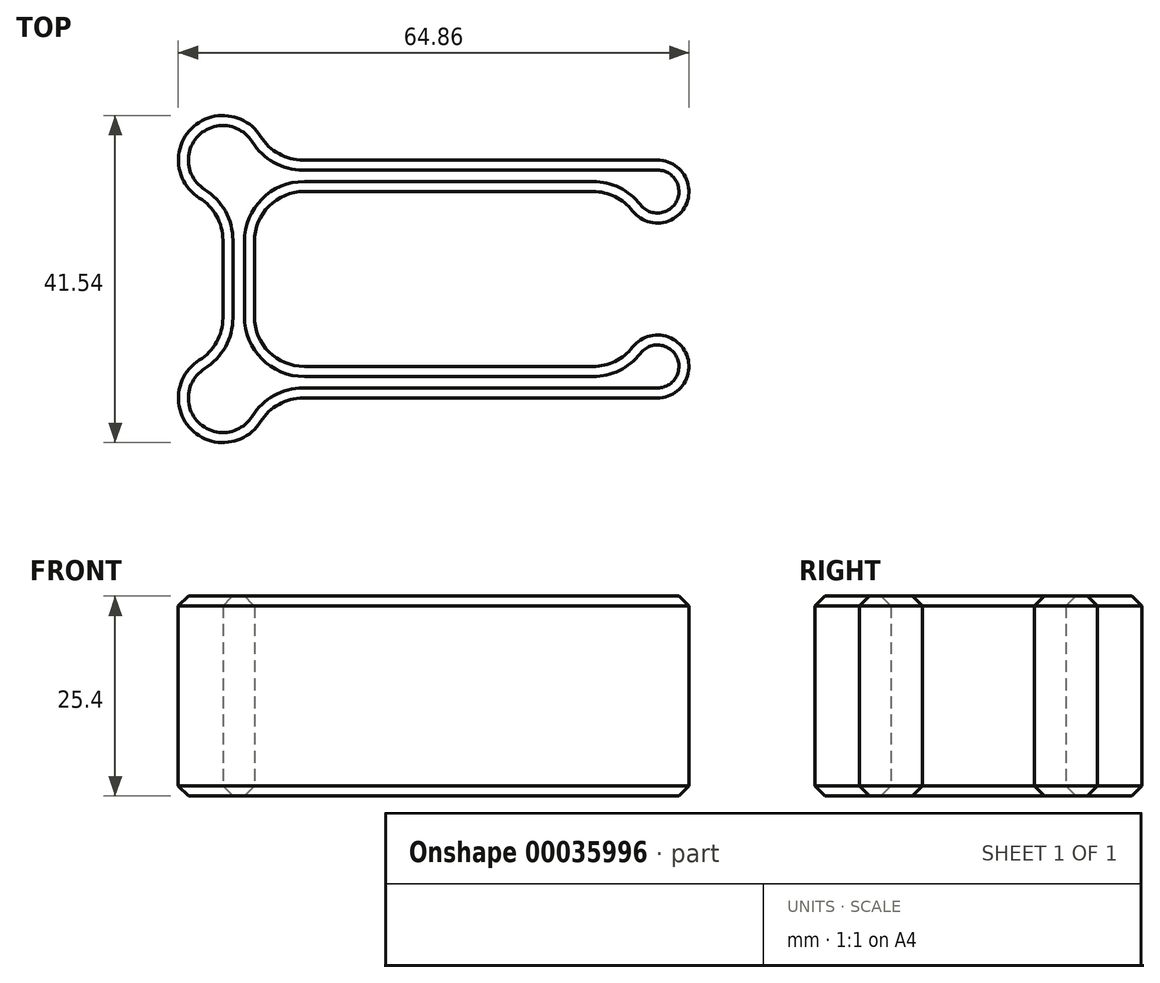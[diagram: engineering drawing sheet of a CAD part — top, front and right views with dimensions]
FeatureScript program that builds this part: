
annotation { "Feature Type Name" : "Feature", "Feature Type Description" : "" }
export const myFeature = defineFeature(function(context is Context, id is Id, definition is map)
    precondition{}
    {
        {
            var Q0;
            Q0=qCreatedBy(makeId("Top.planeOp"),FACE);
            var sketch = newSketch(context, id + "F0", { "sketchPlane" : qUnion([Q0])});
            skLineSegment(sketch, "E0.rect.right", {"start": v(-75.55, 24.4) * mm, "end": v(-75.55, 33.92) * mm});
            skPoint(sketch, "E0.rect.middle", {"position": v(-49.95, 29.16) * mm});
            skArc(sketch, "E1", {"start": v(-74.75, 47.26) * mm, "mid": v(-83.55, 48.27) * mm, "end": v(-82.54, 39.47) * mm});
            skLineSegment(sketch, "E2", {"start": v(-24.35, 44.27) * mm, "end": v(-69.36, 44.27) * mm});
            skLineSegment(sketch, "E3", {"start": v(-32.52, 40.27) * mm, "end": v(-69.2, 40.27) * mm});
            skLineSegment(sketch, "E4", {"start": v(-79.55, 24.24) * mm, "end": v(-79.55, 34.08) * mm});
            skArc(sketch, "E5", {"start": v(-82.54, 18.85) * mm, "mid": v(-83.55, 10.05) * mm, "end": v(-74.75, 11.06) * mm});
            skLineSegment(sketch, "E6", {"start": v(-32.52, 18.05) * mm, "end": v(-69.2, 18.05) * mm});
            skLineSegment(sketch, "E7", {"start": v(-24.35, 14.05) * mm, "end": v(-69.36, 14.05) * mm});
            skArc(sketch, "E8", {"start": v(-27.5, 37.82) * mm, "mid": v(-20.76, 38.51) * mm, "end": v(-24.35, 44.27) * mm});
            skArc(sketch, "E9", {"start": v(-24.35, 14.05) * mm, "mid": v(-20.76, 19.8) * mm, "end": v(-27.5, 20.5) * mm});
            skPoint(sketch, "E10.visualSharp", {"position": v(-73.9, 44.27) * mm});
            skArc(sketch, "E10.filletArc", {"start": v(-74.75, 47.26) * mm, "mid": v(-72.44, 45.07) * mm, "end": v(-69.36, 44.27) * mm});
            skPoint(sketch, "E11.visualSharp", {"position": v(-79.55, 38.62) * mm});
            skArc(sketch, "E11.filletArc", {"start": v(-79.55, 34.08) * mm, "mid": v(-80.35, 37.16) * mm, "end": v(-82.54, 39.47) * mm});
            skPoint(sketch, "E12.visualSharp", {"position": v(-79.55, 19.7) * mm});
            skArc(sketch, "E12.filletArc", {"start": v(-82.54, 18.85) * mm, "mid": v(-80.35, 21.16) * mm, "end": v(-79.55, 24.24) * mm});
            skPoint(sketch, "E13.visualSharp", {"position": v(-73.9, 14.05) * mm});
            skArc(sketch, "E13.filletArc", {"start": v(-69.36, 14.05) * mm, "mid": v(-72.44, 13.25) * mm, "end": v(-74.75, 11.06) * mm});
            skPoint(sketch, "E14.visualSharp", {"position": v(-75.55, 18.05) * mm});
            skArc(sketch, "E14.filletArc", {"start": v(-75.55, 24.4) * mm, "mid": v(-73.69, 19.9) * mm, "end": v(-69.2, 18.05) * mm});
            skPoint(sketch, "E15.visualSharp", {"position": v(-75.55, 40.27) * mm});
            skArc(sketch, "E15.filletArc", {"start": v(-69.2, 40.27) * mm, "mid": v(-73.69, 38.41) * mm, "end": v(-75.55, 33.92) * mm});
            skPoint(sketch, "E16.visualSharp", {"position": v(-28.35, 40.27) * mm});
            skArc(sketch, "E16.filletArc", {"start": v(-27.5, 37.82) * mm, "mid": v(-29.73, 39.63) * mm, "end": v(-32.52, 40.27) * mm});
            skPoint(sketch, "E17.visualSharp", {"position": v(-28.35, 18.05) * mm});
            skArc(sketch, "E17.filletArc", {"start": v(-32.52, 18.05) * mm, "mid": v(-29.73, 18.7) * mm, "end": v(-27.5, 20.5) * mm});
            skSolve(sketch);
        }
        {
            var Q0;
            Q0=makeQuery(id+"F0.imprint","IMPRINT",FACE,{"disambiguationData":[TD([[makeQuery(id+"F0.imprint","IMPRINT",EDGE,{"derivedFrom":sQuery(id+"F0.wireOp",EDGE,"E0.rect.right")}),1.0]])]});
            extrude(context, id + "F1", {"entities" : qUnion([Q0]), "depth" : 25.4 * mm});
        }
        {
            var Q0;
            Q0=makeQuery(id+"F1.opExtrude","CAP_EDGE",EDGE,{"disambiguationData":[OSD([sQuery(id+"F0.wireOp",EDGE,"E4")])],"isStart":false});
            var Q1;
            Q1=makeQuery(id+"F1.opExtrude","CAP_EDGE",EDGE,{"disambiguationData":[OSD([sQuery(id+"F0.wireOp",EDGE,"E12.filletArc")])],"isStart":false});
            var Q2;
            Q2=makeQuery(id+"F1.opExtrude","CAP_EDGE",EDGE,{"disambiguationData":[OSD([sQuery(id+"F0.wireOp",EDGE,"E3")])],"isStart":false});
            var Q3;
            Q3=makeQuery(id+"F1.opExtrude","CAP_EDGE",EDGE,{"disambiguationData":[OSD([sQuery(id+"F0.wireOp",EDGE,"E2")])],"isStart":false});
            var Q4;
            Q4=makeQuery(id+"F1.opExtrude","CAP_EDGE",EDGE,{"disambiguationData":[OSD([sQuery(id+"F0.wireOp",EDGE,"E6")])],"isStart":false});
            var Q5;
            Q5=makeQuery(id+"F1.opExtrude","CAP_EDGE",EDGE,{"disambiguationData":[OSD([sQuery(id+"F0.wireOp",EDGE,"E5")])],"isStart":false});
            var Q6;
            Q6=makeQuery(id+"F1.opExtrude","CAP_EDGE",EDGE,{"disambiguationData":[OSD([sQuery(id+"F0.wireOp",EDGE,"E1")])],"isStart":true});
            var Q7;
            Q7=makeQuery(id+"F1.opExtrude","CAP_EDGE",EDGE,{"disambiguationData":[OSD([sQuery(id+"F0.wireOp",EDGE,"E5")])],"isStart":true});
            var Q8;
            Q8=makeQuery(id+"F1.opExtrude","CAP_EDGE",EDGE,{"disambiguationData":[OSD([sQuery(id+"F0.wireOp",EDGE,"E4")])],"isStart":true});
            var Q9;
            Q9=makeQuery(id+"F1.opExtrude","SWEPT_EDGE",EDGE,{"disambiguationData":[OSD([sQuery(id+"F0.wireOp",EDGE,"E1"),sQuery(id+"F0.wireOp",EDGE,"E11.filletArc")])]});
            var Q10;
            Q10=makeQuery(id+"F1.opExtrude","CAP_EDGE",EDGE,{"disambiguationData":[OSD([sQuery(id+"F0.wireOp",EDGE,"E12.filletArc")])],"isStart":true});
            var Q11;
            Q11=makeQuery(id+"F1.opExtrude","SWEPT_EDGE",EDGE,{"disambiguationData":[OSD([sQuery(id+"F0.wireOp",EDGE,"E2"),sQuery(id+"F0.wireOp",EDGE,"E8")])]});
            var Q12;
            Q12=makeQuery(id+"F1.opExtrude","CAP_EDGE",EDGE,{"disambiguationData":[OSD([sQuery(id+"F0.wireOp",EDGE,"E17.filletArc")])],"isStart":false});
            var Q13;
            Q13=makeQuery(id+"F1.opExtrude","CAP_EDGE",EDGE,{"disambiguationData":[OSD([sQuery(id+"F0.wireOp",EDGE,"E9")])],"isStart":false});
            var Q14;
            Q14=makeQuery(id+"F1.opExtrude","CAP_EDGE",EDGE,{"disambiguationData":[OSD([sQuery(id+"F0.wireOp",EDGE,"E1")])],"isStart":false});
            var Q15;
            Q15=makeQuery(id+"F1.opExtrude","SWEPT_EDGE",EDGE,{"disambiguationData":[OSD([sQuery(id+"F0.wireOp",EDGE,"E4"),sQuery(id+"F0.wireOp",EDGE,"E12.filletArc")])]});
            var Q16;
            Q16=makeQuery(id+"F1.opExtrude","SWEPT_EDGE",EDGE,{"disambiguationData":[OSD([sQuery(id+"F0.wireOp",EDGE,"E4"),sQuery(id+"F0.wireOp",EDGE,"E11.filletArc")])]});
            var Q17;
            Q17=makeQuery(id+"F1.opExtrude","CAP_EDGE",EDGE,{"disambiguationData":[OSD([sQuery(id+"F0.wireOp",EDGE,"E0.rect.right")])],"isStart":false});
            var Q18;
            Q18=makeQuery(id+"F1.opExtrude","SWEPT_EDGE",EDGE,{"disambiguationData":[OSD([sQuery(id+"F0.wireOp",EDGE,"E5"),sQuery(id+"F0.wireOp",EDGE,"E12.filletArc")])]});
            var Q19;
            Q19=makeQuery(id+"F1.opExtrude","CAP_EDGE",EDGE,{"disambiguationData":[OSD([sQuery(id+"F0.wireOp",EDGE,"E15.filletArc")])],"isStart":false});
            var Q20;
            Q20=makeQuery(id+"F1.opExtrude","CAP_EDGE",EDGE,{"disambiguationData":[OSD([sQuery(id+"F0.wireOp",EDGE,"E7")])],"isStart":false});
            var Q21;
            Q21=makeQuery(id+"F1.opExtrude","SWEPT_EDGE",EDGE,{"disambiguationData":[OSD([sQuery(id+"F0.wireOp",EDGE,"E6"),sQuery(id+"F0.wireOp",EDGE,"E17.filletArc")])]});
            var Q22;
            Q22=makeQuery(id+"F1.opExtrude","CAP_EDGE",EDGE,{"disambiguationData":[OSD([sQuery(id+"F0.wireOp",EDGE,"E11.filletArc")])],"isStart":false});
            var Q23;
            Q23=makeQuery(id+"F1.opExtrude","CAP_EDGE",EDGE,{"disambiguationData":[OSD([sQuery(id+"F0.wireOp",EDGE,"E10.filletArc")])],"isStart":false});
            var Q24;
            Q24=makeQuery(id+"F1.opExtrude","CAP_EDGE",EDGE,{"disambiguationData":[OSD([sQuery(id+"F0.wireOp",EDGE,"E14.filletArc")])],"isStart":false});
            var Q25;
            Q25=makeQuery(id+"F1.opExtrude","CAP_EDGE",EDGE,{"disambiguationData":[OSD([sQuery(id+"F0.wireOp",EDGE,"E10.filletArc")])],"isStart":true});
            var Q26;
            Q26=makeQuery(id+"F1.opExtrude","CAP_EDGE",EDGE,{"disambiguationData":[OSD([sQuery(id+"F0.wireOp",EDGE,"E2")])],"isStart":true});
            var Q27;
            Q27=makeQuery(id+"F1.opExtrude","CAP_EDGE",EDGE,{"disambiguationData":[OSD([sQuery(id+"F0.wireOp",EDGE,"E13.filletArc")])],"isStart":false});
            var Q28;
            Q28=makeQuery(id+"F1.opExtrude","CAP_EDGE",EDGE,{"disambiguationData":[OSD([sQuery(id+"F0.wireOp",EDGE,"E17.filletArc")])],"isStart":true});
            var Q29;
            Q29=makeQuery(id+"F1.opExtrude","CAP_EDGE",EDGE,{"disambiguationData":[OSD([sQuery(id+"F0.wireOp",EDGE,"E9")])],"isStart":true});
            var Q30;
            Q30=makeQuery(id+"F1.opExtrude","CAP_EDGE",EDGE,{"disambiguationData":[OSD([sQuery(id+"F0.wireOp",EDGE,"E8")])],"isStart":true});
            var Q31;
            Q31=makeQuery(id+"F1.opExtrude","CAP_EDGE",EDGE,{"disambiguationData":[OSD([sQuery(id+"F0.wireOp",EDGE,"E0.rect.right")])],"isStart":true});
            var Q32;
            Q32=makeQuery(id+"F1.opExtrude","CAP_EDGE",EDGE,{"disambiguationData":[OSD([sQuery(id+"F0.wireOp",EDGE,"E15.filletArc")])],"isStart":true});
            var Q33;
            Q33=makeQuery(id+"F1.opExtrude","SWEPT_EDGE",EDGE,{"disambiguationData":[OSD([sQuery(id+"F0.wireOp",EDGE,"E8"),sQuery(id+"F0.wireOp",EDGE,"E16.filletArc")])]});
            var Q34;
            Q34=makeQuery(id+"F1.opExtrude","SWEPT_EDGE",EDGE,{"disambiguationData":[OSD([sQuery(id+"F0.wireOp",EDGE,"E6"),sQuery(id+"F0.wireOp",EDGE,"E14.filletArc")])]});
            var Q35;
            Q35=makeQuery(id+"F1.opExtrude","SWEPT_EDGE",EDGE,{"disambiguationData":[OSD([sQuery(id+"F0.wireOp",EDGE,"E7"),sQuery(id+"F0.wireOp",EDGE,"E9")])]});
            var Q36;
            Q36=makeQuery(id+"F1.opExtrude","SWEPT_EDGE",EDGE,{"disambiguationData":[OSD([sQuery(id+"F0.wireOp",EDGE,"E7"),sQuery(id+"F0.wireOp",EDGE,"E13.filletArc")])]});
            var Q37;
            Q37=makeQuery(id+"F1.opExtrude","SWEPT_EDGE",EDGE,{"disambiguationData":[OSD([sQuery(id+"F0.wireOp",EDGE,"E0.rect.right"),sQuery(id+"F0.wireOp",EDGE,"E14.filletArc")])]});
            var Q38;
            Q38=makeQuery(id+"F1.opExtrude","SWEPT_EDGE",EDGE,{"disambiguationData":[OSD([sQuery(id+"F0.wireOp",EDGE,"E0.rect.right"),sQuery(id+"F0.wireOp",EDGE,"E15.filletArc")])]});
            var Q39;
            Q39=makeQuery(id+"F1.opExtrude","SWEPT_EDGE",EDGE,{"disambiguationData":[OSD([sQuery(id+"F0.wireOp",EDGE,"E1"),sQuery(id+"F0.wireOp",EDGE,"E10.filletArc")])]});
            var Q40;
            Q40=makeQuery(id+"F1.opExtrude","SWEPT_EDGE",EDGE,{"disambiguationData":[OSD([sQuery(id+"F0.wireOp",EDGE,"E2"),sQuery(id+"F0.wireOp",EDGE,"E10.filletArc")])]});
            var Q41;
            Q41=makeQuery(id+"F1.opExtrude","CAP_EDGE",EDGE,{"disambiguationData":[OSD([sQuery(id+"F0.wireOp",EDGE,"E11.filletArc")])],"isStart":true});
            var Q42;
            Q42=makeQuery(id+"F1.opExtrude","SWEPT_EDGE",EDGE,{"disambiguationData":[OSD([sQuery(id+"F0.wireOp",EDGE,"E3"),sQuery(id+"F0.wireOp",EDGE,"E16.filletArc")])]});
            var Q43;
            Q43=makeQuery(id+"F1.opExtrude","SWEPT_EDGE",EDGE,{"disambiguationData":[OSD([sQuery(id+"F0.wireOp",EDGE,"E3"),sQuery(id+"F0.wireOp",EDGE,"E15.filletArc")])]});
            var Q44;
            Q44=makeQuery(id+"F1.opExtrude","CAP_EDGE",EDGE,{"disambiguationData":[OSD([sQuery(id+"F0.wireOp",EDGE,"E14.filletArc")])],"isStart":true});
            var Q45;
            Q45=makeQuery(id+"F1.opExtrude","CAP_EDGE",EDGE,{"disambiguationData":[OSD([sQuery(id+"F0.wireOp",EDGE,"E6")])],"isStart":true});
            var Q46;
            Q46=makeQuery(id+"F1.opExtrude","CAP_EDGE",EDGE,{"disambiguationData":[OSD([sQuery(id+"F0.wireOp",EDGE,"E16.filletArc")])],"isStart":false});
            var Q47;
            Q47=makeQuery(id+"F1.opExtrude","CAP_EDGE",EDGE,{"disambiguationData":[OSD([sQuery(id+"F0.wireOp",EDGE,"E8")])],"isStart":false});
            var Q48;
            Q48=makeQuery(id+"F1.opExtrude","SWEPT_EDGE",EDGE,{"disambiguationData":[OSD([sQuery(id+"F0.wireOp",EDGE,"E5"),sQuery(id+"F0.wireOp",EDGE,"E13.filletArc")])]});
            var Q49;
            Q49=makeQuery(id+"F1.opExtrude","SWEPT_EDGE",EDGE,{"disambiguationData":[OSD([sQuery(id+"F0.wireOp",EDGE,"E9"),sQuery(id+"F0.wireOp",EDGE,"E17.filletArc")])]});
            var Q50;
            Q50=makeQuery(id+"F1.opExtrude","CAP_EDGE",EDGE,{"disambiguationData":[OSD([sQuery(id+"F0.wireOp",EDGE,"E16.filletArc")])],"isStart":true});
            var Q51;
            Q51=makeQuery(id+"F1.opExtrude","CAP_EDGE",EDGE,{"disambiguationData":[OSD([sQuery(id+"F0.wireOp",EDGE,"E7")])],"isStart":true});
            var Q52;
            Q52=makeQuery(id+"F1.opExtrude","CAP_EDGE",EDGE,{"disambiguationData":[OSD([sQuery(id+"F0.wireOp",EDGE,"E13.filletArc")])],"isStart":true});
            var Q53;
            Q53=makeQuery(id+"F1.opExtrude","CAP_EDGE",EDGE,{"disambiguationData":[OSD([sQuery(id+"F0.wireOp",EDGE,"E3")])],"isStart":true});
            chamfer(context, id + "F2", {"entities" : qUnion([Q0, Q1, Q2, Q3, Q4, Q5, Q6, Q7, Q8, Q9, Q10, Q11, Q12, Q13, Q14, Q15, Q16, Q17, Q18, Q19, Q20, Q21, Q22, Q23, Q24, Q25, Q26, Q27, Q28, Q29, Q30, Q31, Q32, Q33, Q34, Q35, Q36, Q37, Q38, Q39, Q40, Q41, Q42, Q43, Q44, Q45, Q46, Q47, Q48, Q49, Q50, Q51, Q52, Q53]), "width" : 1.27 * mm, "tangentPropagation" : true});
        }
    });
